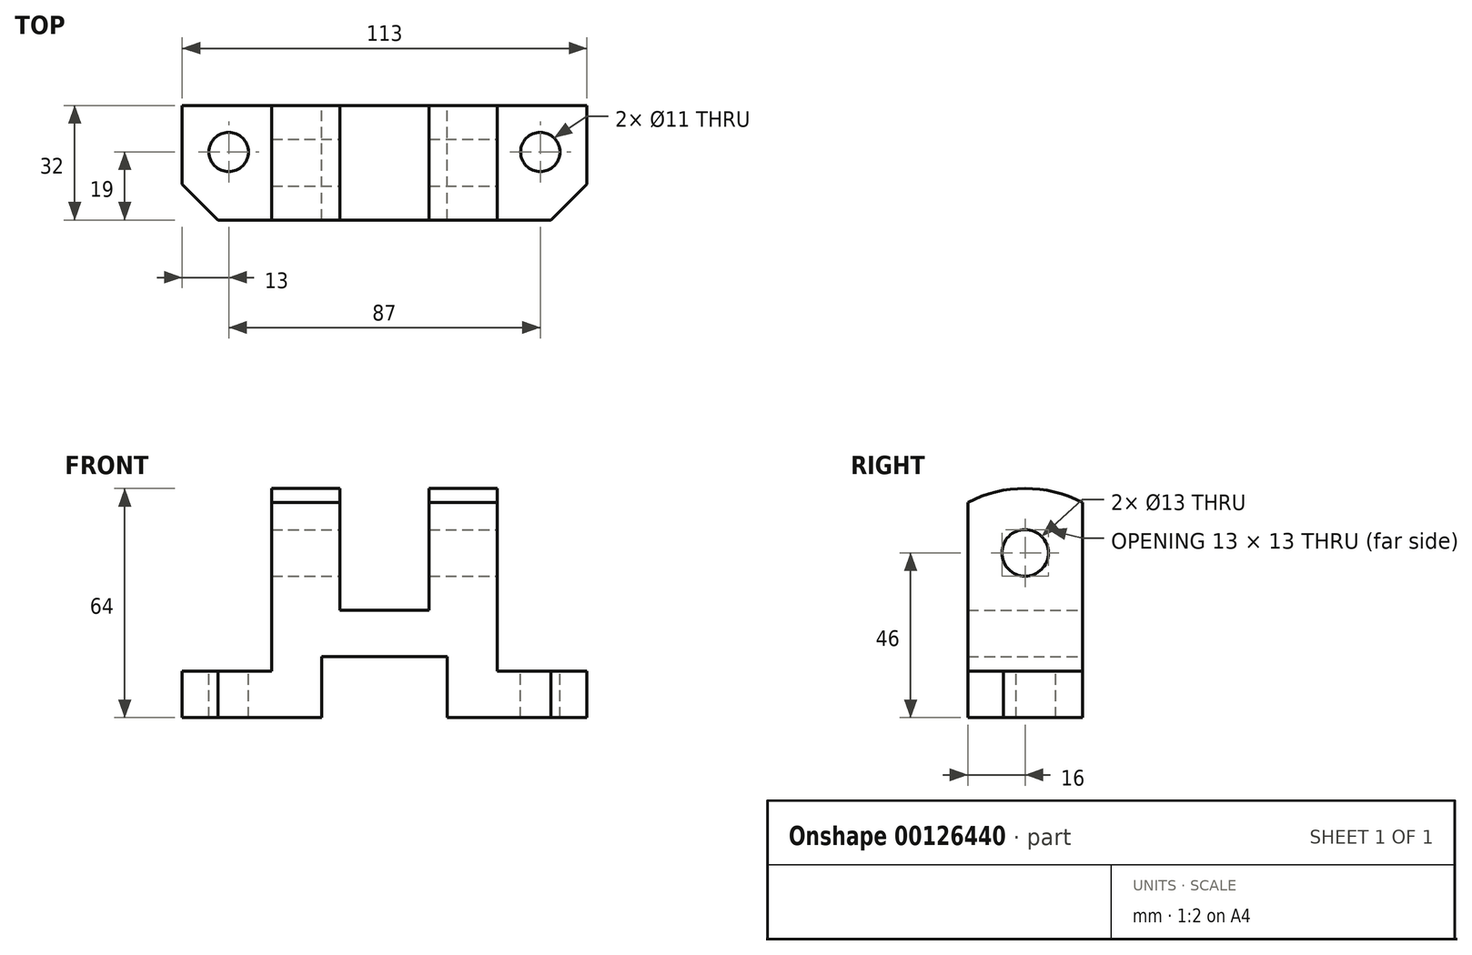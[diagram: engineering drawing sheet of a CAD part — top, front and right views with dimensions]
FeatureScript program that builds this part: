
annotation { "Feature Type Name" : "Feature", "Feature Type Description" : "" }
export const myFeature = defineFeature(function(context is Context, id is Id, definition is map)
    precondition{}
    {
        {
            var Q0;
            Q0=qCreatedBy(makeId("Front.planeOp"),FACE);
            var sketch = newSketch(context, id + "F0", { "sketchPlane" : qUnion([Q0])});
            skLineSegment(sketch, "E0", {"start": v(0, 0) * mm, "end": v(17.5, 0) * mm, "construction": true});
            skLineSegment(sketch, "E1", {"start": v(0, 0) * mm, "end": v(-17.5, 0) * mm, "construction": true});
            skLineSegment(sketch, "E2", {"start": v(-17.5, 0) * mm, "end": v(-56.5, 0) * mm});
            skLineSegment(sketch, "E3", {"start": v(-56.5, 0) * mm, "end": v(-56.5, 13) * mm});
            skLineSegment(sketch, "E4", {"start": v(-56.5, 13) * mm, "end": v(-31.5, 13) * mm});
            skLineSegment(sketch, "E5", {"start": v(-31.5, 13) * mm, "end": v(-31.5, 60.13) * mm});
            skLineSegment(sketch, "E6", {"start": v(-31.5, 60.13) * mm, "end": v(-12.5, 60.13) * mm});
            skLineSegment(sketch, "E7", {"start": v(-12.5, 60.13) * mm, "end": v(-12.5, 30) * mm});
            skLineSegment(sketch, "E8", {"start": v(-12.5, 30) * mm, "end": v(12.5, 30) * mm});
            skLineSegment(sketch, "E9", {"start": v(12.5, 30) * mm, "end": v(12.5, 60.13) * mm});
            skLineSegment(sketch, "E10", {"start": v(12.5, 60.13) * mm, "end": v(31.5, 60.13) * mm});
            skLineSegment(sketch, "E11", {"start": v(31.5, 60.13) * mm, "end": v(31.5, 13) * mm});
            skLineSegment(sketch, "E12", {"start": v(31.5, 13) * mm, "end": v(56.5, 13) * mm});
            skLineSegment(sketch, "E13", {"start": v(56.5, 13) * mm, "end": v(56.5, 0) * mm});
            skLineSegment(sketch, "E14", {"start": v(56.5, 0) * mm, "end": v(17.5, 0) * mm});
            skLineSegment(sketch, "E15", {"start": v(-17.5, 0) * mm, "end": v(-17.5, 17) * mm});
            skLineSegment(sketch, "E16", {"start": v(17.5, 0) * mm, "end": v(17.5, 17) * mm});
            skLineSegment(sketch, "E17", {"start": v(17.5, 17) * mm, "end": v(-17.5, 17) * mm});
            skSolve(sketch);
        }
        {
            var Q0;
            Q0=qSketchRegion(id+"F0",true);
            extrude(context, id + "F1", {"entities" : qUnion([Q0]), "endBound" : BoundingType.SYMMETRIC, "depth" : 32 * mm});
        }
        {
            var Q0;
            Q0=makeQuery(id+"F1.opExtrude","CAP_EDGE",EDGE,{"disambiguationData":[OSD([sQuery(id+"F0.wireOp",EDGE,"E13")])],"isStart":false});
            chamfer(context, id + "F2", {"entities" : qUnion([Q0]), "width" : 10 * mm, "tangentPropagation" : true});
        }
        {
            var Q0;
            Q0=makeQuery(id+"F1.opExtrude","CAP_EDGE",EDGE,{"disambiguationData":[OSD([sQuery(id+"F0.wireOp",EDGE,"E3")])],"isStart":false});
            chamfer(context, id + "F3", {"entities" : qUnion([Q0]), "width" : 10 * mm, "tangentPropagation" : true});
        }
        {
            var Q0;
            Q0=makeQuery(id+"F1.opExtrude","SWEPT_FACE",FACE,{"disambiguationData":[OSD([sQuery(id+"F0.wireOp",EDGE,"E12")])]});
            var sketch = newSketch(context, id + "F4", { "sketchPlane" : qUnion([Q0])});
            skLineSegment(sketch, "E18", {"start": v(56.5, 3) * mm, "end": v(43.5, 3) * mm, "construction": true});
            skLineSegment(sketch, "E19", {"start": v(43.5, 3) * mm, "end": v(43.5, 16) * mm, "construction": true});
            skCircle(sketch, "E20", {"center": v(43.5, 3) * mm, "radius": 5.5 * mm});
            skLineSegment(sketch, "E21", {"start": v(43.5, 3) * mm, "end": v(-43.5, 3) * mm, "construction": true});
            skCircle(sketch, "E22", {"center": v(-43.5, 3) * mm, "radius": 5.5 * mm});
            skSolve(sketch);
        }
        {
            var Q0;
            Q0=qSketchRegion(id+"F4",true);
            var Q1;
            Q1=makeQuery(id+"F1.opExtrude","SWEPT_FACE",FACE,{"disambiguationData":[OSD([sQuery(id+"F0.wireOp",EDGE,"E2")])]});
            extrude(context, id + "F5", {"entities" : qUnion([Q0]), "operationType" : NewBodyOperationType.REMOVE, "endBound" : BoundingType.UP_TO_SURFACE, "oppositeDirection" : true, "endBoundEntityFace" : qUnion([Q1]), "depth" : 25 * mm});
        }
        {
            var Q0;
            Q0=makeQuery(id+"F1.opExtrude","SWEPT_FACE",FACE,{"disambiguationData":[OSD([sQuery(id+"F0.wireOp",EDGE,"E11")])]});
            var sketch = newSketch(context, id + "F6", { "sketchPlane" : qUnion([Q0])});
            skLineSegment(sketch, "E23", {"start": v(0, 0) * mm, "end": v(0, 46) * mm, "construction": true});
            skCircle(sketch, "E24", {"center": v(0, 46) * mm, "radius": 6.5 * mm});
            skSolve(sketch);
        }
        {
            var Q0;
            Q0=qSketchRegion(id+"F6",true);
            var Q1;
            Q1=makeQuery(id+"F1.opExtrude","SWEPT_FACE",FACE,{"disambiguationData":[OSD([sQuery(id+"F0.wireOp",EDGE,"E5")])]});
            extrude(context, id + "F7", {"entities" : qUnion([Q0]), "operationType" : NewBodyOperationType.REMOVE, "endBound" : BoundingType.UP_TO_SURFACE, "oppositeDirection" : true, "endBoundEntityFace" : qUnion([Q1]), "depth" : 25 * mm});
        }
        {
            var Q0;
            Q0=makeQuery(id+"F1.opExtrude","SWEPT_FACE",FACE,{"disambiguationData":[OSD([sQuery(id+"F0.wireOp",EDGE,"E11")])]});
            var sketch = newSketch(context, id + "F8", { "sketchPlane" : qUnion([Q0])});
            skArc(sketch, "E25", {"start": v(16, 60.13) * mm, "mid": v(0, 64) * mm, "end": v(-16, 60.13) * mm});
            skLineSegment(sketch, "E26", {"start": v(16, 60.13) * mm, "end": v(-16, 60.13) * mm});
            skSolve(sketch);
        }
        {
            var Q0;
            Q0=qSketchRegion(id+"F8",true);
            extrude(context, id + "F9", {"entities" : qUnion([Q0]), "operationType" : NewBodyOperationType.ADD, "oppositeDirection" : true, "depth" : 19 * mm});
        }
        {
            var Q0;
            Q0=makeQuery(id+"F1.opExtrude","SWEPT_FACE",FACE,{"disambiguationData":[OSD([sQuery(id+"F0.wireOp",EDGE,"E5")])]});
            var sketch = newSketch(context, id + "F10", { "sketchPlane" : qUnion([Q0])});
            skArc(sketch, "E27", {"start": v(16, 60.13) * mm, "mid": v(0, 64) * mm, "end": v(-16, 60.13) * mm});
            skLineSegment(sketch, "E28", {"start": v(16, 60.13) * mm, "end": v(-16, 60.13) * mm});
            skSolve(sketch);
        }
        {
            var Q0;
            Q0=qSketchRegion(id+"F10",true);
            extrude(context, id + "F11", {"entities" : qUnion([Q0]), "operationType" : NewBodyOperationType.ADD, "oppositeDirection" : true, "depth" : 19 * mm});
        }
    });
